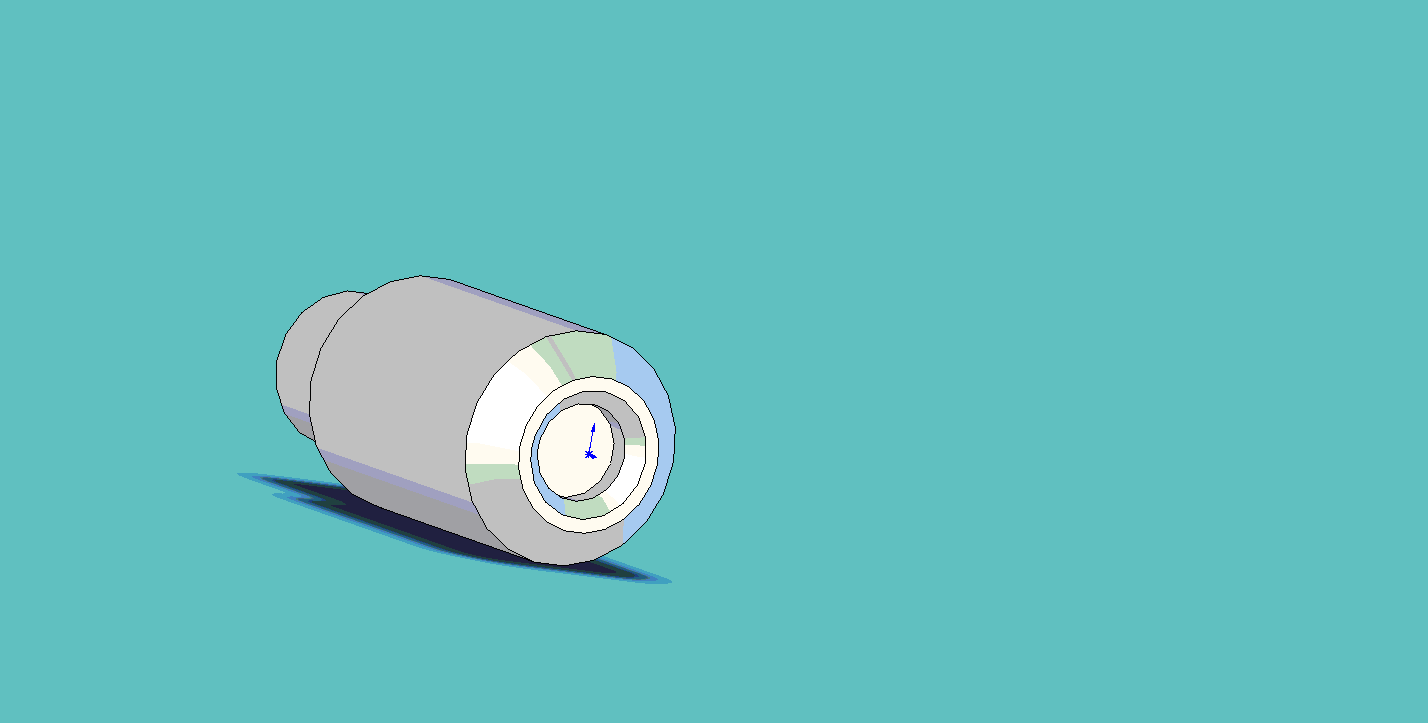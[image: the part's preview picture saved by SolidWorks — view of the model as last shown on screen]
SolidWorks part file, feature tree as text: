
SOLIDWORKS PART (.sldprt)
format: sldprt  version: not decoded by parser v0  size: 153,088 bytes
history: native  units: mm
features: chamfer x4, plane x3, material x1, sketch x1, revolve x1 (+10 scaffold rows collapsed)
feature tree (20):
  scaffold x10  (default folders/planes/origin — collapsed)
  material  "Matériau <non spécifié>"
  plane  "Plan de face"
  plane  "Plan de dessus"
  plane  "Plan de droite"
  sketch  "Esquisse1"  dims[c1.D1=4.0mm c1.D2=4.0mm c1.D3=6.0mm c1.D4=4.0mm c1.D5=13.6mm c1.D6=4.0mm c2.D1=1.0mm c2.D4=2.5mm]
  revolve  "Révolution1"  Angle=360deg
  chamfer  "Chanfrein2"  Distance=1mm Angle=45deg
  chamfer  "Chanfrein3"  Distance=0.4mm Angle=45deg
  chamfer  "Chanfrein4"  Distance=0.2mm Angle=45deg
  chamfer  "Chanfrein5"  Distance=0.5mm Angle=45deg
decode coverage: 6 of 6 modeling features carry decoded parameters
note: suppression state not decoded; provenance and decode notes live in map.json
